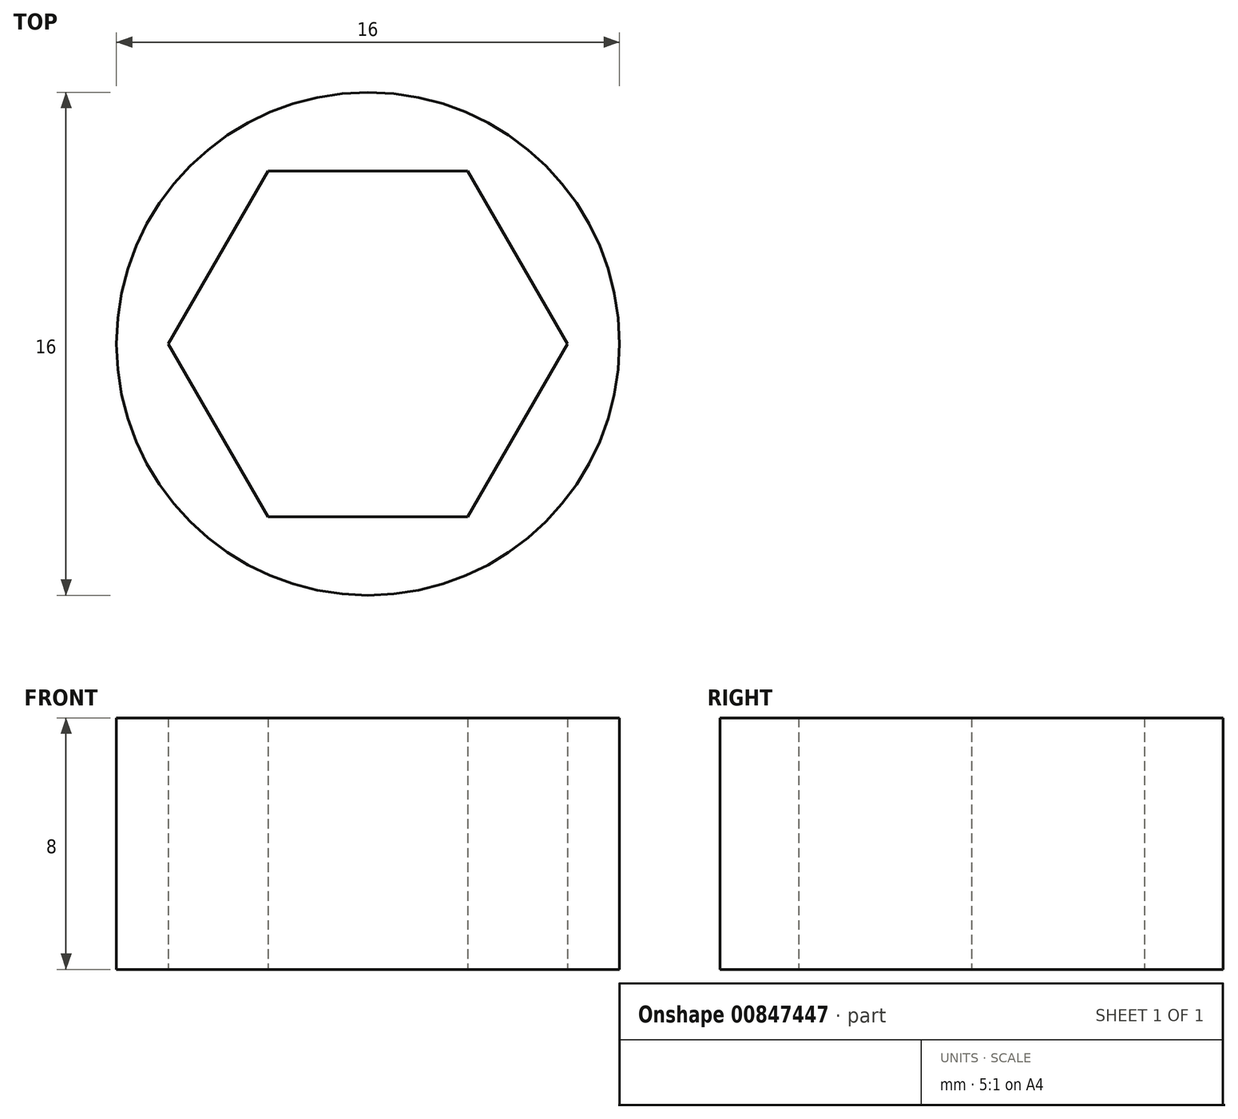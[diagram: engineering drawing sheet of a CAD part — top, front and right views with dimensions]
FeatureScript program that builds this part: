
annotation { "Feature Type Name" : "Feature", "Feature Type Description" : "" }
export const myFeature = defineFeature(function(context is Context, id is Id, definition is map)
    precondition{}
    {
        {
            var Q0;
            Q0=qCreatedBy(makeId("Top.planeOp"),FACE);
            var sketch = newSketch(context, id + "F0", { "sketchPlane" : qUnion([Q0])});
            skCircle(sketch, "E0.cCircle", {"center": v(0, 0) * mm, "radius": 6.35 * mm, "construction": true});
            skLineSegment(sketch, "E0.0", {"start": v(3.18, 5.5) * mm, "end": v(6.35, 0) * mm});
            skLineSegment(sketch, "E0.1", {"start": v(6.35, 0) * mm, "end": v(3.18, -5.5) * mm});
            skLineSegment(sketch, "E0.2", {"start": v(3.18, -5.5) * mm, "end": v(-3.18, -5.5) * mm});
            skLineSegment(sketch, "E0.3", {"start": v(-3.18, -5.5) * mm, "end": v(-6.35, 0) * mm});
            skLineSegment(sketch, "E0.4", {"start": v(-6.35, 0) * mm, "end": v(-3.18, 5.5) * mm});
            skLineSegment(sketch, "E0.5", {"start": v(-3.18, 5.5) * mm, "end": v(3.18, 5.5) * mm});
            skCircle(sketch, "E1", {"center": v(0, 0) * mm, "radius": 8 * mm});
            skSolve(sketch);
        }
        {
            var Q0;
            Q0=makeQuery(id+"F0.imprint","IMPRINT",FACE,{"disambiguationData":[TD([[makeQuery(id+"F0.imprint","IMPRINT",EDGE,{"derivedFrom":sQuery(id+"F0.wireOp",EDGE,"E0.0")}),1.0]])]});
            extrude(context, id + "F1", {"entities" : qUnion([Q0]), "depth" : 8 * mm, "offsetDistance" : 25 * mm});
        }
    });
